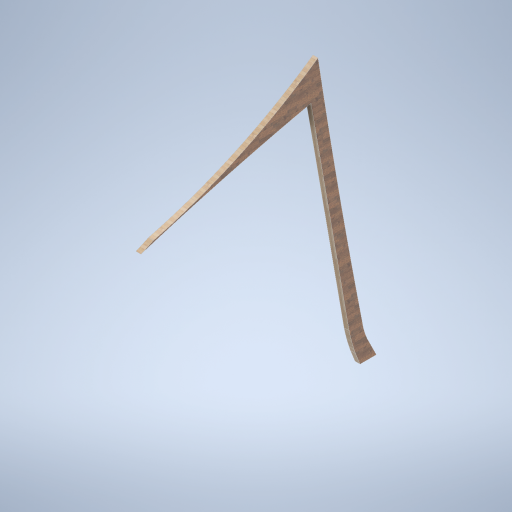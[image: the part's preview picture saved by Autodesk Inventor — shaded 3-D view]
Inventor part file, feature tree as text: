
AUTODESK INVENTOR PART (.ipt)
format: ipt  version: 2024.2 (Build 282272000, 272)  size: 304,640 bytes
history: native  units: in
note: dims shown in document units (in); Inventor stores cm internally (conversion verified against a paired STEP export)
features: other x3, fillet x1, sketch x1
ambient origin geometry x8: Origin, YZ Plane, XZ Plane, XY Plane, X Axis, Y Axis, Z Axis, Center Point
bodies: Body1 (feature_tree)
feature tree (5):
  other  "side_curve_beam_01.ipt"
  fillet  "Fillet1"  Radius=0.3937in
  other  "Solid2::side_curve_beam_01.ipt"
  other  "TaggingFeature1"
  sketch  "Sketch1"  dims[d1=0.3937in]
